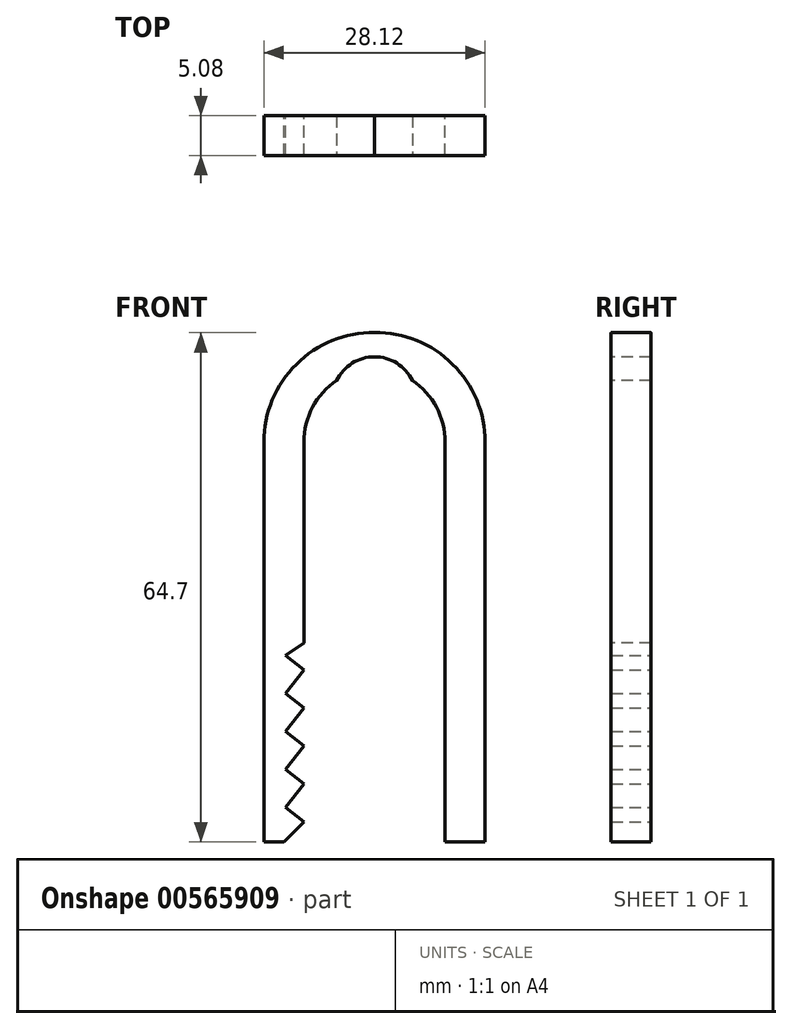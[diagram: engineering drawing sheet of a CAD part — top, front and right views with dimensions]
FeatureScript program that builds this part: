
annotation { "Feature Type Name" : "Feature", "Feature Type Description" : "" }
export const myFeature = defineFeature(function(context is Context, id is Id, definition is map)
    precondition{}
    {
        {
            var Q0;
            Q0=qCreatedBy(makeId("Front.planeOp"),FACE);
            var sketch = newSketch(context, id + "F0", { "sketchPlane" : qUnion([Q0])});
            skLineSegment(sketch, "E0.bottom", {"start": v(-14.06, -34.75) * mm, "end": v(-8.98, -34.75) * mm});
            skLineSegment(sketch, "E0.top", {"start": v(-14.06, 16.05) * mm, "end": v(-8.98, 16.05) * mm});
            skLineSegment(sketch, "E0.left", {"start": v(-14.06, -34.75) * mm, "end": v(-14.06, 16.05) * mm});
            skLineSegment(sketch, "E0.right", {"start": v(-8.98, -34.75) * mm, "end": v(-8.98, 16.05) * mm});
            skArc(sketch, "E1", {"start": v(0, 29.95) * mm, "mid": v(-9.93, 25.93) * mm, "end": v(-14.06, 16.05) * mm});
            skArc(sketch, "E2", {"start": v(0, 25.47) * mm, "mid": v(-6.38, 22.56) * mm, "end": v(-8.98, 16.05) * mm});
            skLineSegment(sketch, "E3", {"start": v(0, 29.95) * mm, "end": v(0, 25.47) * mm});
            skSolve(sketch);
        }
        {
            var Q0;
            Q0 = qSketchRegion(id + "F0", true);
            extrude(context, id + "F1", {"entities" : qUnion([Q0]), "depth" : 5.08 * mm, "offsetDistance" : 25.4 * mm});
        }
        {
            var Q0;
            Q0=makeQuery(id+"F1.opExtrude","SWEPT_BODY",BODY,{"disambiguationData":[OSD([sQuery(id+"F0.wireOp",EDGE,"E0.bottom"),sQuery(id+"F0.wireOp",EDGE,"E0.left"),sQuery(id+"F0.wireOp",EDGE,"E0.right"),sQuery(id+"F0.wireOp",EDGE,"E1"),sQuery(id+"F0.wireOp",EDGE,"E2"),sQuery(id+"F0.wireOp",EDGE,"E3")])]});
            var Q1;
            Q1=qCreatedBy(makeId("Right.planeOp"),FACE);
            mirror(context, id + "F2", {"operationType" : NewBodyOperationType.ADD, "entities" : qUnion([Q0]), "mirrorPlane" : qUnion([Q1])});
        }
        {
            var Q0;
            {var subQ0=makeQuery(id+"F1.opExtrude","CAP_FACE",FACE,{"disambiguationData":[OSD([sQuery(id+"F0.wireOp",EDGE,"E0.bottom"),sQuery(id+"F0.wireOp",EDGE,"E0.left"),sQuery(id+"F0.wireOp",EDGE,"E0.right"),sQuery(id+"F0.wireOp",EDGE,"E1"),sQuery(id+"F0.wireOp",EDGE,"E2"),sQuery(id+"F0.wireOp",EDGE,"E3")])],"isStart":false});Q0=makeQuery(id+"F2.boolean.opBoolean","MERGE",FACE,{"derivedFrom":[subQ0,makeQuery(id+"F2.opPattern","COPY",FACE,{"derivedFrom":subQ0,"instanceName":"1"})]});}
            var sketch = newSketch(context, id + "F3", { "sketchPlane" : qUnion([Q0])});
            skLineSegment(sketch, "E4", {"start": v(-6.03, -7.47) * mm, "end": v(-11.33, -11.03) * mm});
            skLineSegment(sketch, "E5", {"start": v(-11.33, -11.03) * mm, "end": v(-8.98, -12.92) * mm});
            skLineSegment(sketch, "E6", {"start": v(-8.98, -12.92) * mm, "end": v(-11.33, -15.86) * mm});
            skLineSegment(sketch, "E7", {"start": v(-11.33, -15.86) * mm, "end": v(-8.98, -17.74) * mm});
            skLineSegment(sketch, "E8", {"start": v(-8.98, -17.74) * mm, "end": v(-11.33, -20.68) * mm});
            skLineSegment(sketch, "E9", {"start": v(-11.33, -20.68) * mm, "end": v(-8.98, -22.57) * mm});
            skLineSegment(sketch, "E10", {"start": v(-8.98, -22.57) * mm, "end": v(-11.33, -25.5) * mm});
            skLineSegment(sketch, "E11", {"start": v(-11.33, -25.5) * mm, "end": v(-8.98, -27.4) * mm});
            skLineSegment(sketch, "E12", {"start": v(-8.98, -27.4) * mm, "end": v(-11.33, -30.33) * mm});
            skLineSegment(sketch, "E13", {"start": v(-11.33, -30.33) * mm, "end": v(-8.98, -32.22) * mm});
            skLineSegment(sketch, "E14", {"start": v(-8.98, -32.22) * mm, "end": v(-11.52, -34.75) * mm});
            skLineSegment(sketch, "E15", {"start": v(-11.29, -38.71) * mm, "end": v(-6.03, -38.71) * mm});
            skLineSegment(sketch, "E16", {"start": v(-6.03, -38.71) * mm, "end": v(-6.03, -7.47) * mm});
            skLineSegment(sketch, "E17", {"start": v(-11.52, -34.75) * mm, "end": v(-11.29, -38.71) * mm});
            skSolve(sketch);
        }
        {
            var Q0;
            Q0 = qSketchRegion(id + "F3", true);
            extrude(context, id + "F4", {"entities" : qUnion([Q0]), "operationType" : NewBodyOperationType.REMOVE, "endBound" : BoundingType.THROUGH_ALL, "depth" : 25.4 * mm, "offsetDistance" : 25.4 * mm, "hasSecondDirection" : true, "secondDirectionBound" : SecondDirectionBoundingType.THROUGH_ALL, "secondDirectionOppositeDirection" : true, "secondDirectionDepth" : 25.4 * mm});
        }
        {
            var Q0;
            {var subQ0=makeQuery(id+"F1.opExtrude","CAP_FACE",FACE,{"disambiguationData":[OSD([sQuery(id+"F0.wireOp",EDGE,"E0.bottom"),sQuery(id+"F0.wireOp",EDGE,"E0.left"),sQuery(id+"F0.wireOp",EDGE,"E0.right"),sQuery(id+"F0.wireOp",EDGE,"E1"),sQuery(id+"F0.wireOp",EDGE,"E2"),sQuery(id+"F0.wireOp",EDGE,"E3")])],"isStart":false});Q0=makeQuery(id+"F2.boolean.opBoolean","MERGE",FACE,{"derivedFrom":[subQ0,makeQuery(id+"F2.opPattern","COPY",FACE,{"derivedFrom":subQ0,"instanceName":"1"})]});}
            var sketch = newSketch(context, id + "F5", { "sketchPlane" : qUnion([Q0])});
            skCircle(sketch, "E18", {"center": v(0, 21.52) * mm, "radius": 5.36 * mm});
            skSolve(sketch);
        }
        {
            var Q0;
            {var subQ0=sQuery(id+"F5.wireOp",EDGE,"E18");var subQ1=makeQuery(id+"F1.opExtrude","CAP_EDGE",EDGE,{"disambiguationData":[OSD([sQuery(id+"F0.wireOp",EDGE,"E2")])],"isStart":false});var subQ2=makeQuery(id+"F5.imprint","INTERSECT",VERTEX,{"derivedFrom":[subQ1,subQ0]});Q0=makeQuery(id+"F5.imprint","IMPRINT",FACE,{"disambiguationData":[TD([[makeQuery(id+"F5.imprint","IMPRINT",EDGE,{"disambiguationData":[TD([[subQ2,1.0]])],"derivedFrom":subQ0}),1.0]])]});}
            var Q1;
            Q1=sQuery(id+"F5.wireOp",EDGE,"E18");
            extrude(context, id + "F6", {"entities" : qUnion([Q0]), "operationType" : NewBodyOperationType.REMOVE, "surfaceEntities" : qUnion([Q1]), "endBound" : BoundingType.THROUGH_ALL, "oppositeDirection" : true, "depth" : 25.4 * mm, "offsetDistance" : 25.4 * mm, "hasSecondDirection" : true, "secondDirectionBound" : SecondDirectionBoundingType.THROUGH_ALL, "secondDirectionOppositeDirection" : false, "secondDirectionDepth" : 25.4 * mm});
        }
    });
